# Revit family: Haworth_Masters_PersonalStorageTower
name_source: partatom
category: Furniture Systems
revit_build: Autodesk Revit 2018 (Build: 20170223_1515(x64)
units: mm (PartAtom-declared; Revit-internal decimal feet)

## family parameters
Always vertical = Yes
Cut with Voids When Loaded = No
OmniClass Number = 23.40.70.14.64.21
OmniClass Title = Systems Furniture
Part Type = Normal
Room Calculation Point = No
Round Connector Dimension = Use Diameter
Shared = No
Work Plane-Based = No

## types (1)
- 24d 24w 69h - File File File
    Actual Depth = 23 5/8"
    Actual Height = 69"
    Actual Width = 24"
    Assembly Code = E2020200
    Bar Pull = No
    Classic Pull = No
    Description = Haworth - Masters - Personal Storage Tower
    Door Height = 65 5/8"
    Door Height 2 = 29 1/4"
    Door Width = 9"
    Drawer 1 Height = 12"
    Drawer 2 Height = 12"
    Drawer 3 = Yes
    Drawer 3 Height = 12"
    Drawer 4 Height = 5 15/16"
    Drawer Width = 14 7/8"
    File File = No
    File File File = Yes
    Finger Pull = No
    Five High = Yes
    Linear Pull = Yes
    Manufacturer = Haworth
    Model = Haworth - Masters - Personal Storage Tower
    Pull Finish = Haworth _ Metal _ Chrome
    Pull Height Centerline = 51"
    Pull Height Centerline 2 = 14 5/8"
    Revision Number = 2
    Shelf Depth = 13 1/2"
    Shelf Width = 22 1/8"
    Six High = No
    Size = Verify Final Dim. w/ Haworth
    Standard Heights = 69 in, 81.625in.
    Sustainability Info = http://www.haworth.com
    URL = http://www.haworth.com
    URL - Product = http://www.haworth.com
    Warranty = http://www.haworth.com

## geometry (parser evidence)
native form markers: Sweep x11
no freeform markers — native parametric forms only
